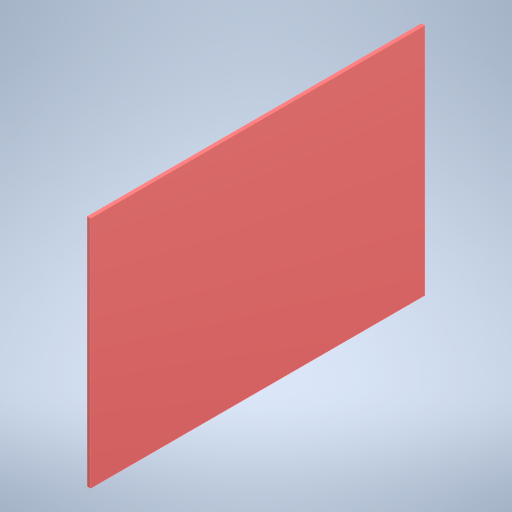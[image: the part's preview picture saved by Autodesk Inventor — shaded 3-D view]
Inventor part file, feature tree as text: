
AUTODESK INVENTOR PART (.ipt)
format: ipt  version: 2024.3 (Build 283343000, 343)  size: 182,784 bytes
history: native  units: mm
features: extrude x1, sketch x1
ambient origin geometry x8: Origin, YZ Plane, XZ Plane, XY Plane, X Axis, Y Axis, Z Axis, Center Point
bodies: Solid1 (feature_tree)
feature tree (2):
  extrude  "Extrusion1"  Depth=100.0mm
  sketch  "Sketch1"  dims[d0=70.0mm d1=100.0mm d2=1.0mm d3=0.0mm]
